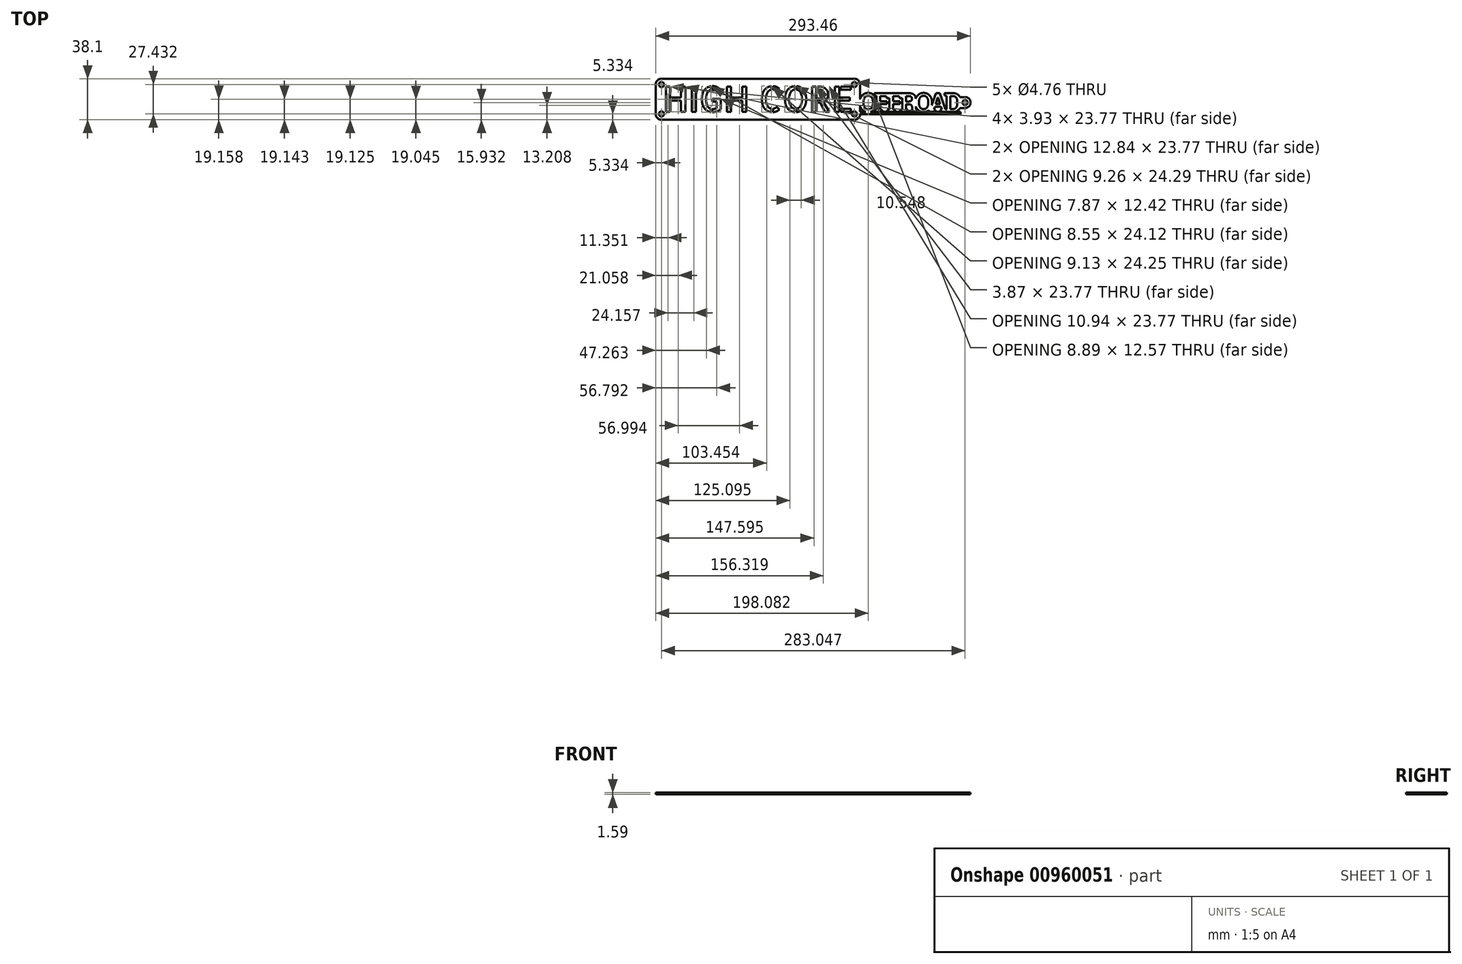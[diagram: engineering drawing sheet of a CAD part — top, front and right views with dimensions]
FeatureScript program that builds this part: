
annotation { "Feature Type Name" : "Feature", "Feature Type Description" : "" }
export const myFeature = defineFeature(function(context is Context, id is Id, definition is map)
    precondition{}
    {
        {
            var Q0;
            Q0=qCreatedBy(makeId("Top.planeOp"),FACE);
            var sketch = newSketch(context, id + "F0", { "sketchPlane" : qUnion([Q0])});
            skLineSegment(sketch, "E0.bottom", {"start": v(95.25, -19.05) * mm, "end": v(-95.25, -19.05) * mm});
            skLineSegment(sketch, "E0.top", {"start": v(95.25, 19.05) * mm, "end": v(-95.25, 19.05) * mm});
            skLineSegment(sketch, "E0.left", {"start": v(95.25, -19.05) * mm, "end": v(95.25, 19.05) * mm});
            skLineSegment(sketch, "E0.right", {"start": v(-95.25, -19.05) * mm, "end": v(-95.25, 19.05) * mm});
            skPoint(sketch, "E0.middle", {"position": v(0, 0) * mm});
            skSolve(sketch);
        }
        {
            var Q0;
            Q0=makeQuery(id+"F0.imprint","IMPRINT",FACE,{"disambiguationData":[TD([[makeQuery(id+"F0.imprint","IMPRINT",EDGE,{"derivedFrom":sQuery(id+"F0.wireOp",EDGE,"E0.bottom")}),-1.0]])]});
            extrude(context, id + "F1", {"entities" : qUnion([Q0]), "depth" : 1.59 * mm, "offsetDistance" : 25.4 * mm});
        }
        {
            var Q0;
            Q0=makeQuery(id+"F1.opExtrude","CAP_FACE",FACE,{"disambiguationData":[OSD([sQuery(id+"F0.wireOp",EDGE,"E0.bottom"),sQuery(id+"F0.wireOp",EDGE,"E0.top"),sQuery(id+"F0.wireOp",EDGE,"E0.left"),sQuery(id+"F0.wireOp",EDGE,"E0.right")])],"isStart":false});
            var sketch = newSketch(context, id + "F2", { "sketchPlane" : qUnion([Q0])});
            skText(sketch, "E1", { "text": "HIGH CORE", "fontName": "AllertaStencil-Regular.ttf"});
            skPoint(sketch, "E2", {"position": v(0, 0) * mm});
            skLineSegment(sketch, "E3", {"start": v(-89.92, 0) * mm, "end": v(0, 0) * mm, "construction": true});
            skLineSegment(sketch, "E4", {"start": v(0, 0) * mm, "end": v(89.92, 0) * mm, "construction": true});
            skLineSegment(sketch, "E5", {"start": v(-95.25, 19.05) * mm, "end": v(-88.39, 12.19) * mm, "construction": true});
            skLineSegment(sketch, "E6", {"start": v(-89.92, 0) * mm, "end": v(-89.92, 13.72) * mm, "construction": true});
            skCircle(sketch, "E7", {"center": v(-89.92, 13.72) * mm, "radius": 2.38 * mm});
            skCircle(sketch, "E8.MirrorC", {"center": v(-89.92, -13.72) * mm, "radius": 2.38 * mm});
            skCircle(sketch, "E9.MirrorC", {"center": v(89.92, 13.72) * mm, "radius": 2.38 * mm});
            skCircle(sketch, "E10.MirrorC", {"center": v(89.92, -13.72) * mm, "radius": 2.38 * mm});
            const initialGuessF2  = {"E1": [-0.0889, -0.01189, 1, 0, 0.02378]};
            skSetInitialGuess(sketch, initialGuessF2);
            skSolve(sketch);
        }
        {
            var Q0;
            Q0 = qSketchRegion(id + "F2", true);
            extrude(context, id + "F3", {"entities" : qUnion([Q0]), "operationType" : NewBodyOperationType.REMOVE, "oppositeDirection" : true, "depth" : 25.4 * mm, "offsetDistance" : 25.4 * mm});
        }
        {
            var Q0;
            Q0=makeQuery(id+"F1.opExtrude","SWEPT_EDGE",EDGE,{"disambiguationData":[OSD([sQuery(id+"F0.wireOp",EDGE,"E0.top"),sQuery(id+"F0.wireOp",EDGE,"E0.right")])]});
            var Q1;
            Q1=makeQuery(id+"F1.opExtrude","SWEPT_EDGE",EDGE,{"disambiguationData":[OSD([sQuery(id+"F0.wireOp",EDGE,"E0.bottom"),sQuery(id+"F0.wireOp",EDGE,"E0.right")])]});
            var Q2;
            Q2=makeQuery(id+"F1.opExtrude","SWEPT_EDGE",EDGE,{"disambiguationData":[OSD([sQuery(id+"F0.wireOp",EDGE,"E0.top"),sQuery(id+"F0.wireOp",EDGE,"E0.left")])]});
            var Q3;
            Q3=makeQuery(id+"F1.opExtrude","SWEPT_EDGE",EDGE,{"disambiguationData":[OSD([sQuery(id+"F0.wireOp",EDGE,"E0.bottom"),sQuery(id+"F0.wireOp",EDGE,"E0.left")])]});
            fillet(context, id + "F4", {"entities" : qUnion([Q0, Q1, Q2, Q3]), "radius" : 5.08 * mm, "tangentPropagation" : true, "allowEdgeOverflow" : false});
        }
        {
            var Q0;
            Q0=makeQuery(id+"F1.opExtrude","CAP_FACE",FACE,{"disambiguationData":[OSD([sQuery(id+"F0.wireOp",EDGE,"E0.bottom"),sQuery(id+"F0.wireOp",EDGE,"E0.top"),sQuery(id+"F0.wireOp",EDGE,"E0.left"),sQuery(id+"F0.wireOp",EDGE,"E0.right")])],"isStart":false});
            var sketch = newSketch(context, id + "F5", { "sketchPlane" : qUnion([Q0])});
            skPoint(sketch, "E11", {"position": v(93.37, -3.45) * mm});
            skText(sketch, "E12", { "text": "O", "fontName": "RobotoSlab-Bold.ttf"});
            skText(sketch, "E13", { "text": "F", "fontName": "RobotoSlab-Bold.ttf"});
            skText(sketch, "E14", { "text": "F", "fontName": "RobotoSlab-Bold.ttf"});
            skText(sketch, "E15", { "text": "R", "fontName": "RobotoSlab-Bold.ttf"});
            skText(sketch, "E16", { "text": "O", "fontName": "RobotoSlab-Bold.ttf"});
            skText(sketch, "E17", { "text": "A", "fontName": "RobotoSlab-Bold.ttf"});
            skText(sketch, "E18", { "text": "D", "fontName": "RobotoSlab-Bold.ttf"});
            skLineSegment(sketch, "E19", {"start": v(86.7, -11.89) * mm, "end": v(188.8, -11.89) * mm});
            skLineSegment(sketch, "E20.0", {"start": v(95.25, -13.97) * mm, "end": v(95.25, 13.97) * mm});
            skLineSegment(sketch, "E21", {"start": v(95.25, -13.97) * mm, "end": v(188.8, -13.97) * mm});
            skLineSegment(sketch, "E22", {"start": v(188.8, -11.89) * mm, "end": v(188.8, -13.97) * mm});
            skLineSegment(sketch, "E23", {"start": v(95.25, -13.97) * mm, "end": v(95.25, -11.89) * mm});
            skLineSegment(sketch, "E24", {"start": v(95.25, -11.89) * mm, "end": v(188.8, -11.89) * mm});
            const initialGuessF5  = {"E12": [0.09406, -0.01189, 1, 0, 0.01778], "E13": [0.10804, -0.01189, 1, 0, 0.01778], "E14": [0.12013, -0.01189, 1, 0, 0.01778], "E15": [0.1322, -0.01189, 1, 0, 0.01778], "E16": [0.14582, -0.01166, 1, 0, 0.01755], "E17": [0.15894, -0.01186, 1, 0, 0.01778], "E18": [0.17335, -0.01186, 1, 0, 0.01778]};
            skSetInitialGuess(sketch, initialGuessF5);
            skSolve(sketch);
        }
        {
            var Q0;
            {var subQ2=sQuery(id+"F5.wireOp",EDGE,"E17.sketch_text.stroke-5");Q0=makeQuery(id+"F5.imprint","IMPRINT",FACE,{"disambiguationData":[TD([[makeQuery(id+"F5.imprint","IMPRINT",EDGE,{"derivedFrom":subQ2}),-1.0]])]});}
            var Q1;
            {var subQ6=sQuery(id+"F5.wireOp",EDGE,"E17.sketch_text.stroke-5");Q1=makeQuery(id+"F5.imprint","IMPRINT",FACE,{"disambiguationData":[TD([[makeQuery(id+"F5.imprint","IMPRINT",EDGE,{"derivedFrom":subQ6}),1.0]])]});}
            var Q2;
            {var subQ15=sQuery(id+"F5.wireOp",EDGE,"E17.sketch_text.stroke-2");Q2=makeQuery(id+"F5.imprint","IMPRINT",FACE,{"disambiguationData":[TD([[makeQuery(id+"F5.imprint","IMPRINT",EDGE,{"derivedFrom":subQ15}),-1.0]])]});}
            var Q3;
            {var subQ0=sQuery(id+"F5.wireOp",EDGE,"E16.sketch_text.stroke-1");var subQ1=sQuery(id+"F5.wireOp",EDGE,"E16.sketch_text.stroke-0");var subQ2=makeQuery(id+"F5.imprint","INTERSECT",VERTEX,{"derivedFrom":[subQ1,subQ0]});Q3=makeQuery(id+"F5.imprint","IMPRINT",FACE,{"disambiguationData":[TD([[makeQuery(id+"F5.imprint","IMPRINT",EDGE,{"disambiguationData":[TD([[subQ2,1.0]])],"derivedFrom":subQ1}),1.0]])]});}
            var Q4;
            {var subQ0=sQuery(id+"F5.wireOp",EDGE,"E17.sketch_text.stroke-15");var subQ1=sQuery(id+"F5.wireOp",EDGE,"E16.sketch_text.stroke-1");var subQ2=makeQuery(id+"F5.imprint","INTERSECT",VERTEX,{"derivedFrom":[subQ1,subQ0]});Q4=makeQuery(id+"F5.imprint","IMPRINT",FACE,{"disambiguationData":[TD([[makeQuery(id+"F5.imprint","IMPRINT",EDGE,{"disambiguationData":[TD([[subQ2,1.0]])],"derivedFrom":subQ1}),-1.0]])]});}
            var Q5;
            {var subQ9=sQuery(id+"F5.wireOp",EDGE,"E16.sketch_text.stroke-4");Q5=makeQuery(id+"F5.imprint","IMPRINT",FACE,{"disambiguationData":[TD([[makeQuery(id+"F5.imprint","IMPRINT",EDGE,{"derivedFrom":subQ9}),-1.0]])]});}
            var Q6;
            {var subQ0=sQuery(id+"F5.wireOp",EDGE,"E17.sketch_text.stroke-1");var subQ1=sQuery(id+"F5.wireOp",EDGE,"E16.sketch_text.stroke-0");var subQ2=makeQuery(id+"F5.imprint","INTERSECT",VERTEX,{"disambiguationData":[OD(0.0)],"derivedFrom":[subQ1,subQ0]});Q6=makeQuery(id+"F5.imprint","IMPRINT",FACE,{"disambiguationData":[TD([[makeQuery(id+"F5.imprint","IMPRINT",EDGE,{"disambiguationData":[TD([[subQ2,-1.0]])],"derivedFrom":subQ1}),-1.0]])]});}
            var Q7;
            {var subQ7=sQuery(id+"F5.wireOp",EDGE,"E14.sketch_text.stroke-5");Q7=makeQuery(id+"F5.imprint","IMPRINT",FACE,{"disambiguationData":[TD([[makeQuery(id+"F5.imprint","IMPRINT",EDGE,{"derivedFrom":subQ7}),1.0]])]});}
            var Q8;
            {var subQ0=sQuery(id+"F5.wireOp",EDGE,"E15.sketch_text.stroke-2");var subQ1=sQuery(id+"F5.wireOp",EDGE,"E15.sketch_text.stroke-1");var subQ2=makeQuery(id+"F5.imprint","INTERSECT",VERTEX,{"derivedFrom":[subQ1,subQ0]});Q8=makeQuery(id+"F5.imprint","IMPRINT",FACE,{"disambiguationData":[TD([[makeQuery(id+"F5.imprint","IMPRINT",EDGE,{"disambiguationData":[TD([[subQ2,1.0]])],"derivedFrom":subQ1}),-1.0]])]});}
            var Q9;
            {var subQ0=sQuery(id+"F5.wireOp",EDGE,"E16.sketch_text.stroke-3");var subQ1=sQuery(id+"F5.wireOp",EDGE,"E15.sketch_text.stroke-5");var subQ2=makeQuery(id+"F5.imprint","INTERSECT",VERTEX,{"disambiguationData":[OD(0.0)],"derivedFrom":[subQ1,subQ0]});Q9=makeQuery(id+"F5.imprint","IMPRINT",FACE,{"disambiguationData":[TD([[makeQuery(id+"F5.imprint","IMPRINT",EDGE,{"disambiguationData":[TD([[subQ2,-1.0]])],"derivedFrom":subQ1}),-1.0]])]});}
            var Q10;
            {var subQ2=sQuery(id+"F5.wireOp",EDGE,"E14.sketch_text.stroke-5");Q10=makeQuery(id+"F5.imprint","IMPRINT",FACE,{"disambiguationData":[TD([[makeQuery(id+"F5.imprint","IMPRINT",EDGE,{"derivedFrom":subQ2}),-1.0]])]});}
            var Q11;
            {var subQ1=sQuery(id+"F5.wireOp",EDGE,"E13.sketch_text.stroke-5");Q11=makeQuery(id+"F5.imprint","IMPRINT",FACE,{"disambiguationData":[TD([[makeQuery(id+"F5.imprint","IMPRINT",EDGE,{"derivedFrom":subQ1}),1.0]])]});}
            var Q12;
            {var subQ2=sQuery(id+"F5.wireOp",EDGE,"E13.sketch_text.stroke-5");Q12=makeQuery(id+"F5.imprint","IMPRINT",FACE,{"disambiguationData":[TD([[makeQuery(id+"F5.imprint","IMPRINT",EDGE,{"derivedFrom":subQ2}),-1.0]])]});}
            var Q13;
            {var subQ8=sQuery(id+"F5.wireOp",EDGE,"E12.sketch_text.stroke-9");Q13=makeQuery(id+"F5.imprint","IMPRINT",FACE,{"disambiguationData":[TD([[makeQuery(id+"F5.imprint","IMPRINT",EDGE,{"derivedFrom":subQ8}),1.0]])]});}
            var Q14;
            {var subQ0=sQuery(id+"F5.wireOp",EDGE,"E12.sketch_text.stroke-6");Q14=makeQuery(id+"F5.imprint","IMPRINT",FACE,{"disambiguationData":[TD([[makeQuery(id+"F5.imprint","IMPRINT",EDGE,{"derivedFrom":subQ0}),-1.0]])]});}
            var Q15;
            {var subQ5=sQuery(id+"F5.wireOp",EDGE,"E15.sketch_text.stroke-3");Q15=makeQuery(id+"F5.imprint","IMPRINT",FACE,{"disambiguationData":[TD([[makeQuery(id+"F5.imprint","IMPRINT",EDGE,{"derivedFrom":subQ5}),1.0]])]});}
            extrude(context, id + "F6", {"entities" : qUnion([Q0, Q1, Q2, Q3, Q4, Q5, Q6, Q7, Q8, Q9, Q10, Q11, Q12, Q13, Q14, Q15]), "operationType" : NewBodyOperationType.ADD, "oppositeDirection" : true, "depth" : 1.59 * mm, "offsetDistance" : 25.4 * mm});
        }
        {
            var Q0;
            Q0=makeQuery(id+"F6.opExtrude","CAP_FACE",FACE,{"disambiguationData":[OSD([sQuery(id+"F5.wireOp",EDGE,"E12.sketch_text.stroke-0"),sQuery(id+"F5.wireOp",EDGE,"E12.sketch_text.stroke-8"),sQuery(id+"F5.wireOp",EDGE,"E12.sketch_text.stroke-9"),sQuery(id+"F5.wireOp",EDGE,"E13.sketch_text.stroke-0"),sQuery(id+"F5.wireOp",EDGE,"E13.sketch_text.stroke-1"),sQuery(id+"F5.wireOp",EDGE,"E13.sketch_text.stroke-2"),sQuery(id+"F5.wireOp",EDGE,"E13.sketch_text.stroke-3"),sQuery(id+"F5.wireOp",EDGE,"E13.sketch_text.stroke-4"),sQuery(id+"F5.wireOp",EDGE,"E13.sketch_text.stroke-6"),sQuery(id+"F5.wireOp",EDGE,"E13.sketch_text.stroke-7"),sQuery(id+"F5.wireOp",EDGE,"E13.sketch_text.stroke-8"),sQuery(id+"F5.wireOp",EDGE,"E13.sketch_text.stroke-9"),sQuery(id+"F5.wireOp",EDGE,"E13.sketch_text.stroke-10"),sQuery(id+"F5.wireOp",EDGE,"E13.sketch_text.stroke-11"),sQuery(id+"F5.wireOp",EDGE,"E13.sketch_text.stroke-12"),sQuery(id+"F5.wireOp",EDGE,"E13.sketch_text.stroke-13"),sQuery(id+"F5.wireOp",EDGE,"E13.sketch_text.stroke-14"),sQuery(id+"F5.wireOp",EDGE,"E13.sketch_text.stroke-15"),sQuery(id+"F5.wireOp",EDGE,"E13.sketch_text.stroke-17"),sQuery(id+"F5.wireOp",EDGE,"E14.sketch_text.stroke-0"),sQuery(id+"F5.wireOp",EDGE,"E14.sketch_text.stroke-1"),sQuery(id+"F5.wireOp",EDGE,"E14.sketch_text.stroke-4"),sQuery(id+"F5.wireOp",EDGE,"E14.sketch_text.stroke-6"),sQuery(id+"F5.wireOp",EDGE,"E14.sketch_text.stroke-7"),sQuery(id+"F5.wireOp",EDGE,"E14.sketch_text.stroke-8"),sQuery(id+"F5.wireOp",EDGE,"E14.sketch_text.stroke-9"),sQuery(id+"F5.wireOp",EDGE,"E14.sketch_text.stroke-10"),sQuery(id+"F5.wireOp",EDGE,"E14.sketch_text.stroke-11"),sQuery(id+"F5.wireOp",EDGE,"E14.sketch_text.stroke-12"),sQuery(id+"F5.wireOp",EDGE,"E14.sketch_text.stroke-13"),sQuery(id+"F5.wireOp",EDGE,"E14.sketch_text.stroke-14"),sQuery(id+"F5.wireOp",EDGE,"E14.sketch_text.stroke-15"),sQuery(id+"F5.wireOp",EDGE,"E14.sketch_text.stroke-17"),sQuery(id+"F5.wireOp",EDGE,"E15.sketch_text.stroke-0"),sQuery(id+"F5.wireOp",EDGE,"E15.sketch_text.stroke-1"),sQuery(id+"F5.wireOp",EDGE,"E15.sketch_text.stroke-5"),sQuery(id+"F5.wireOp",EDGE,"E15.sketch_text.stroke-6"),sQuery(id+"F5.wireOp",EDGE,"E15.sketch_text.stroke-7"),sQuery(id+"F5.wireOp",EDGE,"E15.sketch_text.stroke-8"),sQuery(id+"F5.wireOp",EDGE,"E15.sketch_text.stroke-9"),sQuery(id+"F5.wireOp",EDGE,"E15.sketch_text.stroke-10"),sQuery(id+"F5.wireOp",EDGE,"E15.sketch_text.stroke-12"),sQuery(id+"F5.wireOp",EDGE,"E15.sketch_text.stroke-13"),sQuery(id+"F5.wireOp",EDGE,"E15.sketch_text.stroke-14"),sQuery(id+"F5.wireOp",EDGE,"E15.sketch_text.stroke-15"),sQuery(id+"F5.wireOp",EDGE,"E15.sketch_text.stroke-16"),sQuery(id+"F5.wireOp",EDGE,"E15.sketch_text.stroke-17"),sQuery(id+"F5.wireOp",EDGE,"E15.sketch_text.stroke-18"),sQuery(id+"F5.wireOp",EDGE,"E15.sketch_text.stroke-19"),sQuery(id+"F5.wireOp",EDGE,"E15.sketch_text.stroke-20"),sQuery(id+"F5.wireOp",EDGE,"E15.sketch_text.stroke-22"),sQuery(id+"F5.wireOp",EDGE,"E15.sketch_text.stroke-23"),sQuery(id+"F5.wireOp",EDGE,"E15.sketch_text.stroke-24"),sQuery(id+"F5.wireOp",EDGE,"E15.sketch_text.stroke-27"),sQuery(id+"F5.wireOp",EDGE,"E15.sketch_text.stroke-28"),sQuery(id+"F5.wireOp",EDGE,"E15.sketch_text.stroke-29"),sQuery(id+"F5.wireOp",EDGE,"E15.sketch_text.stroke-30"),sQuery(id+"F5.wireOp",EDGE,"E15.sketch_text.stroke-31"),sQuery(id+"F5.wireOp",EDGE,"E15.sketch_text.stroke-32"),sQuery(id+"F5.wireOp",EDGE,"E15.sketch_text.stroke-33"),sQuery(id+"F5.wireOp",EDGE,"E15.sketch_text.stroke-34"),sQuery(id+"F5.wireOp",EDGE,"E15.sketch_text.stroke-35"),sQuery(id+"F5.wireOp",EDGE,"E16.sketch_text.stroke-0"),sQuery(id+"F5.wireOp",EDGE,"E16.sketch_text.stroke-1"),sQuery(id+"F5.wireOp",EDGE,"E16.sketch_text.stroke-2"),sQuery(id+"F5.wireOp",EDGE,"E16.sketch_text.stroke-3"),sQuery(id+"F5.wireOp",EDGE,"E16.sketch_text.stroke-5"),sQuery(id+"F5.wireOp",EDGE,"E16.sketch_text.stroke-6"),sQuery(id+"F5.wireOp",EDGE,"E16.sketch_text.stroke-7"),sQuery(id+"F5.wireOp",EDGE,"E16.sketch_text.stroke-8"),sQuery(id+"F5.wireOp",EDGE,"E16.sketch_text.stroke-9"),sQuery(id+"F5.wireOp",EDGE,"E16.sketch_text.stroke-10"),sQuery(id+"F5.wireOp",EDGE,"E16.sketch_text.stroke-11"),sQuery(id+"F5.wireOp",EDGE,"E16.sketch_text.stroke-12"),sQuery(id+"F5.wireOp",EDGE,"E16.sketch_text.stroke-13"),sQuery(id+"F5.wireOp",EDGE,"E16.sketch_text.stroke-14"),sQuery(id+"F5.wireOp",EDGE,"E16.sketch_text.stroke-15"),sQuery(id+"F5.wireOp",EDGE,"E16.sketch_text.stroke-16"),sQuery(id+"F5.wireOp",EDGE,"E16.sketch_text.stroke-17"),sQuery(id+"F5.wireOp",EDGE,"E16.sketch_text.stroke-18"),sQuery(id+"F5.wireOp",EDGE,"E16.sketch_text.stroke-19"),sQuery(id+"F5.wireOp",EDGE,"E17.sketch_text.stroke-1"),sQuery(id+"F5.wireOp",EDGE,"E17.sketch_text.stroke-2"),sQuery(id+"F5.wireOp",EDGE,"E17.sketch_text.stroke-3"),sQuery(id+"F5.wireOp",EDGE,"E17.sketch_text.stroke-4"),sQuery(id+"F5.wireOp",EDGE,"E17.sketch_text.stroke-6"),sQuery(id+"F5.wireOp",EDGE,"E17.sketch_text.stroke-7"),sQuery(id+"F5.wireOp",EDGE,"E17.sketch_text.stroke-8"),sQuery(id+"F5.wireOp",EDGE,"E17.sketch_text.stroke-9"),sQuery(id+"F5.wireOp",EDGE,"E17.sketch_text.stroke-10"),sQuery(id+"F5.wireOp",EDGE,"E17.sketch_text.stroke-11"),sQuery(id+"F5.wireOp",EDGE,"E17.sketch_text.stroke-12"),sQuery(id+"F5.wireOp",EDGE,"E17.sketch_text.stroke-13"),sQuery(id+"F5.wireOp",EDGE,"E17.sketch_text.stroke-14"),sQuery(id+"F5.wireOp",EDGE,"E17.sketch_text.stroke-15"),sQuery(id+"F5.wireOp",EDGE,"E17.sketch_text.stroke-16"),sQuery(id+"F5.wireOp",EDGE,"E17.sketch_text.stroke-17"),sQuery(id+"F5.wireOp",EDGE,"E17.sketch_text.stroke-18"),sQuery(id+"F5.wireOp",EDGE,"E17.sketch_text.stroke-19"),sQuery(id+"F5.wireOp",EDGE,"E18.sketch_text.stroke-0"),sQuery(id+"F5.wireOp",EDGE,"E18.sketch_text.stroke-1"),sQuery(id+"F5.wireOp",EDGE,"E18.sketch_text.stroke-2"),sQuery(id+"F5.wireOp",EDGE,"E18.sketch_text.stroke-3"),sQuery(id+"F5.wireOp",EDGE,"E18.sketch_text.stroke-4"),sQuery(id+"F5.wireOp",EDGE,"E18.sketch_text.stroke-5"),sQuery(id+"F5.wireOp",EDGE,"E18.sketch_text.stroke-7"),sQuery(id+"F5.wireOp",EDGE,"E18.sketch_text.stroke-8"),sQuery(id+"F5.wireOp",EDGE,"E18.sketch_text.stroke-9"),sQuery(id+"F5.wireOp",EDGE,"E18.sketch_text.stroke-10"),sQuery(id+"F5.wireOp",EDGE,"E18.sketch_text.stroke-11"),sQuery(id+"F5.wireOp",EDGE,"E18.sketch_text.stroke-12"),sQuery(id+"F5.wireOp",EDGE,"E18.sketch_text.stroke-13"),sQuery(id+"F5.wireOp",EDGE,"E18.sketch_text.stroke-14"),sQuery(id+"F5.wireOp",EDGE,"E18.sketch_text.stroke-15"),sQuery(id+"F5.wireOp",EDGE,"E18.sketch_text.stroke-16"),sQuery(id+"F5.wireOp",EDGE,"E18.sketch_text.stroke-17"),sQuery(id+"F5.wireOp",EDGE,"E18.sketch_text.stroke-18"),sQuery(id+"F5.wireOp",EDGE,"E18.sketch_text.stroke-19"),sQuery(id+"F5.wireOp",EDGE,"E18.sketch_text.stroke-20"),sQuery(id+"F5.wireOp",EDGE,"E24")])],"isStart":true});
            var sketch = newSketch(context, id + "F7", { "sketchPlane" : qUnion([Q0])});
            skLineSegment(sketch, "E25", {"start": v(189.32, -3.09) * mm, "end": v(193.13, -3.09) * mm, "construction": true});
            skCircle(sketch, "E26", {"center": v(193.13, -3.09) * mm, "radius": 2.38 * mm});
            skCircle(sketch, "E27", {"center": v(193.13, -3.09) * mm, "radius": 5.08 * mm});
            skLineSegment(sketch, "E28", {"start": v(193.13, 2) * mm, "end": v(187.45, 2) * mm});
            skLineSegment(sketch, "E29", {"start": v(193.13, -8.17) * mm, "end": v(187.5, -8.17) * mm});
            skLineSegment(sketch, "E30", {"start": v(187.5, -8.17) * mm, "end": v(187.45, 2) * mm});
            skSolve(sketch);
        }
        {
            var Q0;
            Q0=makeQuery(id+"F5.imprint","IMPRINT",FACE,{"disambiguationData":[TD([[makeQuery(id+"F5.imprint","IMPRINT",EDGE,{"derivedFrom":sQuery(id+"F5.wireOp",EDGE,"E21")}),1.0]])]});
            var Q1;
            {var subQ0=sQuery(id+"F5.wireOp",EDGE,"E12.sketch_text.stroke-2");var subQ1=sQuery(id+"F5.wireOp",EDGE,"E12.sketch_text.stroke-1");var subQ2=makeQuery(id+"F5.imprint","INTERSECT",VERTEX,{"derivedFrom":[subQ1,subQ0]});Q1=makeQuery(id+"F5.imprint","IMPRINT",FACE,{"disambiguationData":[TD([[makeQuery(id+"F5.imprint","IMPRINT",EDGE,{"disambiguationData":[TD([[subQ2,1.0]])],"derivedFrom":subQ1}),-1.0]])]});}
            var Q2;
            {var subQ0=sQuery(id+"F7.wireOp",EDGE,"E28");var subQ1=sQuery(id+"F7.wireOp",EDGE,"E27");var subQ2=makeQuery(id+"F7.imprint","INTERSECT",VERTEX,{"derivedFrom":[subQ1,subQ0]});Q2=makeQuery(id+"F7.imprint","IMPRINT",FACE,{"disambiguationData":[TD([[makeQuery(id+"F7.imprint","IMPRINT",EDGE,{"disambiguationData":[TD([[subQ2,-1.0]])],"derivedFrom":subQ1}),-1.0]])]});}
            var Q3;
            Q3=makeQuery(id+"F7.imprint","IMPRINT",FACE,{"disambiguationData":[TD([[makeQuery(id+"F7.imprint","IMPRINT",EDGE,{"derivedFrom":sQuery(id+"F7.wireOp",EDGE,"E26")}),-1.0]])]});
            var Q4;
            {var subQ0=sQuery(id+"F7.wireOp",EDGE,"E29");var subQ1=sQuery(id+"F7.wireOp",EDGE,"E27");var subQ2=makeQuery(id+"F7.imprint","INTERSECT",VERTEX,{"derivedFrom":[subQ1,subQ0]});Q4=makeQuery(id+"F7.imprint","IMPRINT",FACE,{"disambiguationData":[TD([[makeQuery(id+"F7.imprint","IMPRINT",EDGE,{"disambiguationData":[TD([[subQ2,1.0]])],"derivedFrom":subQ1}),-1.0]])]});}
            extrude(context, id + "F8", {"entities" : qUnion([Q0, Q1, Q2, Q3, Q4]), "operationType" : NewBodyOperationType.ADD, "oppositeDirection" : true, "depth" : 1.59 * mm, "offsetDistance" : 25.4 * mm});
        }
    });
